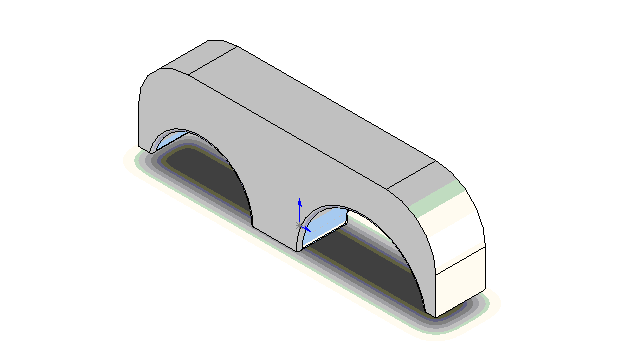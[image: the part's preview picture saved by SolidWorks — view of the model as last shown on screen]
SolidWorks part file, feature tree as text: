
SOLIDWORKS PART (.sldprt)
format: sldprt  version: not decoded by parser v0  size: 228,352 bytes
history: native  units: mm
features: sketch x3, fillet x2, extrude x1, hole x1 (+11 scaffold rows collapsed)
feature tree (18):
  scaffold x11  (default folders/planes/origin — collapsed)
  sketch  "Sketch1"  dims[c1.D1=~29.818825mm c1.D4=12.7mm c1.D5=16.002mm c2.D1=3.175mm c2.D2=3.175mm c2.D3=25.4mm c2.D6=76.2mm c2.D7=41.275mm c2.D8=~0.79375mm c2.D9=~0.79375mm c2.D10=19.05mm c3.D2=60.325mm c3.D3=25.4mm c3.D8=22.225mm]
  extrude  "Extrude1"  Depth=12.7mm
  fillet  "Fillet1"  Radius=12.7mm
  fillet  "Fillet2"  Radius=0.762mm
  hole  "1/4-20 Tapped Hole1"  Diameter=5.1054mm Depth=19.05mm
  sketch  "3DSketch1"  dims[D1=6.35mm D2=~41.396935mm]
  sketch  "Sketch2"  dims[hole-wizard template sketch: 29 standard entries collapsed; hole parameters kept: c8.Tap Drill Depth=19.05mm c8.Thread Major Dia.=6.35mm c8.Thread Depth=9.652mm c8.D5=~14.816244mm c8.Drill Angle=118.0deg]
decode coverage: 7 of 7 modeling features carry decoded parameters
note: ~ marks probable driven/reference dimensions
note: suppression state not decoded; provenance and decode notes live in map.json
